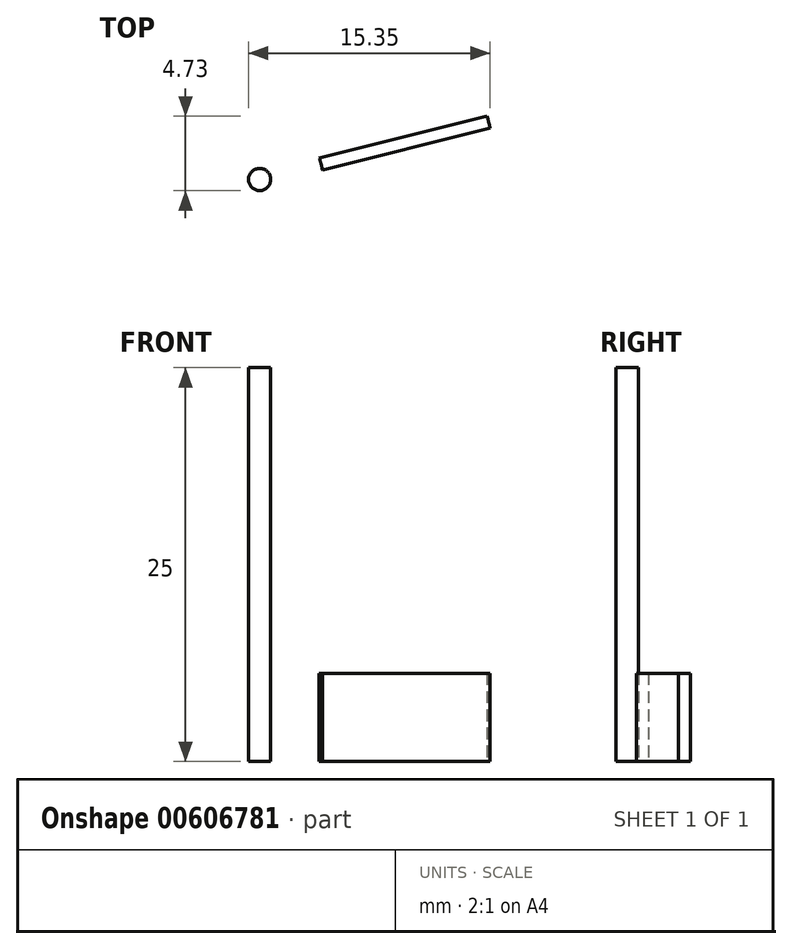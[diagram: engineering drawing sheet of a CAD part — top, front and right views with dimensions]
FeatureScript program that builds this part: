
annotation { "Feature Type Name" : "Feature", "Feature Type Description" : "" }
export const myFeature = defineFeature(function(context is Context, id is Id, definition is map)
    precondition{}
    {
        {
            var Q0;
            Q0=qCreatedBy(makeId("Top.planeOp"),FACE);
            var sketch = newSketch(context, id + "F0", { "sketchPlane" : qUnion([Q0])});
            skCircle(sketch, "E0", {"center": v(0, 0) * mm, "radius": 4.03 * mm});
            skCircle(sketch, "E1.cCircle", {"center": v(0, 0) * mm, "radius": 4.03 * mm, "construction": true});
            skLineSegment(sketch, "E1.0", {"start": v(2.8, -2.9) * mm, "end": v(-3.9, -0.98) * mm});
            skLineSegment(sketch, "E1.1", {"start": v(-3.9, -0.98) * mm, "end": v(1.1, 3.87) * mm});
            skLineSegment(sketch, "E1.2", {"start": v(1.1, 3.87) * mm, "end": v(2.8, -2.9) * mm});
            skLineSegment(sketch, "E2.0", {"start": v(-3.9, -0.98) * mm, "end": v(-2.8, 2.9) * mm});
            skLineSegment(sketch, "E2.1", {"start": v(-2.8, 2.9) * mm, "end": v(1.1, 3.87) * mm});
            skLineSegment(sketch, "E2.2", {"start": v(1.1, 3.87) * mm, "end": v(3.9, 0.98) * mm});
            skLineSegment(sketch, "E2.3", {"start": v(3.9, 0.98) * mm, "end": v(2.8, -2.9) * mm});
            skLineSegment(sketch, "E2.4", {"start": v(2.8, -2.9) * mm, "end": v(-1.1, -3.87) * mm});
            skLineSegment(sketch, "E2.5", {"start": v(-1.1, -3.87) * mm, "end": v(-3.9, -0.98) * mm});
            skCircle(sketch, "E3", {"center": v(0, 0) * mm, "radius": 15 * mm});
            skLineSegment(sketch, "E4", {"start": v(-2.5, 3.16) * mm, "end": v(-3.07, 2.6) * mm});
            skLineSegment(sketch, "E5", {"start": v(0.72, 3.96) * mm, "end": v(1.49, 3.74) * mm});
            skLineSegment(sketch, "E6", {"start": v(3.79, 1.36) * mm, "end": v(3.98, 0.58) * mm});
            skLineSegment(sketch, "E7", {"start": v(3.07, -2.6) * mm, "end": v(2.5, -3.16) * mm});
            skLineSegment(sketch, "E8", {"start": v(-1.49, -3.74) * mm, "end": v(-0.72, -3.96) * mm});
            skLineSegment(sketch, "E9", {"start": v(-3.98, -0.58) * mm, "end": v(-3.79, -1.37) * mm});
            skLineSegment(sketch, "E10", {"start": v(-2.5, 3.16) * mm, "end": v(-10.14, 11.06) * mm});
            skLineSegment(sketch, "E11", {"start": v(-3.07, 2.6) * mm, "end": v(-10.71, 10.5) * mm});
            skLineSegment(sketch, "E12", {"start": v(0.72, 3.96) * mm, "end": v(3.74, 14.53) * mm});
            skLineSegment(sketch, "E13", {"start": v(1.49, 3.74) * mm, "end": v(4.5, 14.3) * mm});
            skLineSegment(sketch, "E14", {"start": v(3.79, 1.36) * mm, "end": v(14.45, 4.02) * mm});
            skLineSegment(sketch, "E15", {"start": v(3.98, 0.58) * mm, "end": v(14.64, 3.25) * mm});
            skLineSegment(sketch, "E16", {"start": v(3.07, -2.6) * mm, "end": v(10.71, -10.5) * mm});
            skLineSegment(sketch, "E17", {"start": v(2.5, -3.16) * mm, "end": v(10.14, -11.06) * mm});
            skLineSegment(sketch, "E18", {"start": v(-0.72, -3.96) * mm, "end": v(-3.74, -14.53) * mm});
            skLineSegment(sketch, "E19", {"start": v(-1.49, -3.74) * mm, "end": v(-4.5, -14.3) * mm});
            skLineSegment(sketch, "E20", {"start": v(-3.79, -1.37) * mm, "end": v(-14.45, -4.04) * mm});
            skLineSegment(sketch, "E21", {"start": v(-3.98, -0.58) * mm, "end": v(-14.64, -3.25) * mm});
            skCircle(sketch, "E22", {"center": v(0, 0) * mm, "radius": 0.7 * mm});
            skSolve(sketch);
        }
        {
            var Q0;
            {var subQ2=sQuery(id+"F0.wireOp",EDGE,"E14");Q0=makeQuery(id+"F0.imprint","IMPRINT",FACE,{"disambiguationData":[TD([[makeQuery(id+"F0.imprint","IMPRINT",EDGE,{"derivedFrom":subQ2}),-1.0]])]});}
            extrude(context, id + "F1", {"entities" : qUnion([Q0]), "depth" : 5.6 * mm, "offsetDistance" : 25 * mm});
        }
        {
            var Q0;
            Q0=makeQuery(id+"F0.imprint","IMPRINT",FACE,{"disambiguationData":[TD([[makeQuery(id+"F0.imprint","IMPRINT",EDGE,{"derivedFrom":sQuery(id+"F0.wireOp",EDGE,"E22")}),1.0]])]});
            extrude(context, id + "F2", {"entities" : qUnion([Q0]), "depth" : 25 * mm, "offsetDistance" : 25 * mm});
        }
    });
